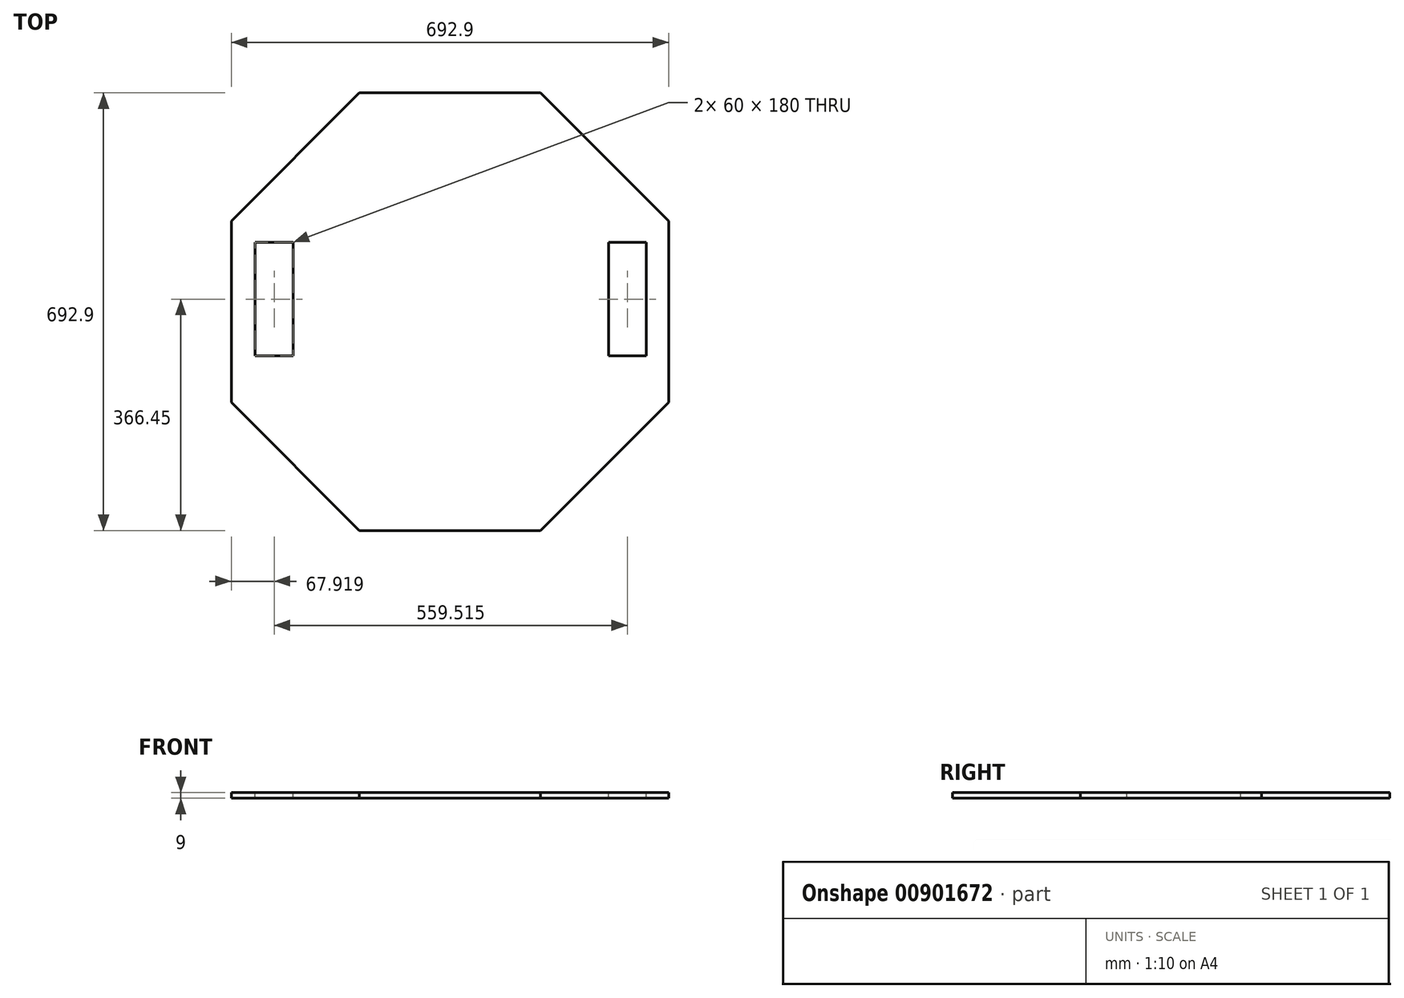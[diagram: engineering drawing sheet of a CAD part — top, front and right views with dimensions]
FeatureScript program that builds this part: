
annotation { "Feature Type Name" : "Feature", "Feature Type Description" : "" }
export const myFeature = defineFeature(function(context is Context, id is Id, definition is map)
    precondition{}
    {
        {
            var Q0;
            Q0=qCreatedBy(makeId("Top.planeOp"),FACE);
            var sketch = newSketch(context, id + "F0", { "sketchPlane" : qUnion([Q0])});
            skCircle(sketch, "E0.cCircle", {"center": v(0, 0) * mm, "radius": 375 * mm, "construction": true});
            skLineSegment(sketch, "E0.0", {"start": v(-143.5, 346.45) * mm, "end": v(143.5, 346.45) * mm});
            skLineSegment(sketch, "E0.1", {"start": v(143.5, 346.45) * mm, "end": v(346.45, 143.5) * mm});
            skLineSegment(sketch, "E0.2", {"start": v(346.45, 143.5) * mm, "end": v(346.45, -143.5) * mm});
            skLineSegment(sketch, "E0.3", {"start": v(346.45, -143.5) * mm, "end": v(143.5, -346.45) * mm});
            skLineSegment(sketch, "E0.4", {"start": v(143.5, -346.45) * mm, "end": v(-143.5, -346.45) * mm});
            skLineSegment(sketch, "E0.5", {"start": v(-143.5, -346.45) * mm, "end": v(-346.45, -143.5) * mm});
            skLineSegment(sketch, "E0.6", {"start": v(-346.45, -143.5) * mm, "end": v(-346.45, 143.5) * mm});
            skLineSegment(sketch, "E0.7", {"start": v(-346.45, 143.5) * mm, "end": v(-143.5, 346.45) * mm});
            skSolve(sketch);
        }
        {
            var Q0;
            Q0=makeQuery(id+"F0.imprint","IMPRINT",FACE,{"disambiguationData":[TD([[makeQuery(id+"F0.imprint","IMPRINT",EDGE,{"derivedFrom":sQuery(id+"F0.wireOp",EDGE,"E0.0")}),-1.0]])]});
            extrude(context, id + "F1", {"entities" : qUnion([Q0]), "depth" : 9 * mm, "offsetDistance" : 25.4 * mm});
        }
        {
            var Q0;
            Q0=makeQuery(id+"F1.opExtrude","CAP_FACE",FACE,{"disambiguationData":[OSD([sQuery(id+"F0.wireOp",EDGE,"E0.0"),sQuery(id+"F0.wireOp",EDGE,"E0.1"),sQuery(id+"F0.wireOp",EDGE,"E0.2"),sQuery(id+"F0.wireOp",EDGE,"E0.3"),sQuery(id+"F0.wireOp",EDGE,"E0.4"),sQuery(id+"F0.wireOp",EDGE,"E0.5"),sQuery(id+"F0.wireOp",EDGE,"E0.6"),sQuery(id+"F0.wireOp",EDGE,"E0.7")])],"isStart":false});
            var sketch = newSketch(context, id + "F2", { "sketchPlane" : qUnion([Q0])});
            skLineSegment(sketch, "E1.bottom", {"start": v(-308.53, 110) * mm, "end": v(-248.53, 110) * mm});
            skLineSegment(sketch, "E1.top", {"start": v(-308.53, -70) * mm, "end": v(-248.53, -70) * mm});
            skLineSegment(sketch, "E1.left", {"start": v(-308.53, 110) * mm, "end": v(-308.53, -70) * mm});
            skLineSegment(sketch, "E1.right", {"start": v(-248.53, 110) * mm, "end": v(-248.53, -70) * mm});
            skLineSegment(sketch, "E2.bottom", {"start": v(250.98, 110) * mm, "end": v(310.98, 110) * mm});
            skLineSegment(sketch, "E2.top", {"start": v(250.98, -70) * mm, "end": v(310.98, -70) * mm});
            skLineSegment(sketch, "E2.left", {"start": v(250.98, 110) * mm, "end": v(250.98, -70) * mm});
            skLineSegment(sketch, "E2.right", {"start": v(310.98, 110) * mm, "end": v(310.98, -70) * mm});
            skSolve(sketch);
        }
        {
            var Q0;
            Q0 = qSketchRegion(id + "F2", true);
            extrude(context, id + "F3", {"entities" : qUnion([Q0]), "operationType" : NewBodyOperationType.REMOVE, "endBound" : BoundingType.THROUGH_ALL, "oppositeDirection" : true, "depth" : 25 * mm, "offsetDistance" : 25 * mm});
        }
    });
